# Revit family: Drain_Floor_Round-Zurn-Z415C
name_source: partatom
category: Plumbing Fixtures
units: mm (PartAtom-declared; Revit-internal decimal feet)

## family parameters
Always vertical = Yes
Cut with Voids When Loaded = No
Maintain Annotation Orientation = No
OmniClass Number = 23.70.50.21.24.14
OmniClass Title = Deck Waste Water Drains
Part Type = Normal
Room Calculation Point = No
Round Connector Dimension = Use Radius
Shared = No
Work Plane-Based = No

## types (80) — shared parameters
Assembly Code = D2030300
CW Connection = No
Default Elevation = 30 "
Description = BODY ASSEMBLY W/ “TYPE C” STRAINER
HW Connection = No
Manufacturer = Zurn Water, LLC
Manufacurer Brand = Zurn
Material Main = Iron - Zurn - Cast - Painted - Blue
Modified Date = 12/05/2025
Product Documentation Link = https://files.zurn.com
Product Installation Sheet URL = https://files.zurn.com
Product Page URL = https://www.zurn.com
Product data url = https://bimobject.com
URL = www.zurn.com
Vent Connection = No
Waste Connection = Yes
zero-valued in all types: CWFU, HWFU, WFU

## per-type parameters (varying)
| type | Approx. Wt. Lbs. | Body Height (E) | Grate Radius | Model | Pipe Size 'A' (Inner Diameter) | Pipe Size 'A' (Inner Radius) | Pipe Size 'A' (Nominal Diameter) | Pipe Size 'A' (Nominal Radius) | Pipe Size 'A' (Outer Diameter) | Pipe Size 'A' (Outer Radius) | Strainer Diameter (B) | Strainer Material | Strainer Open Area | Type Comments |
| ZN415C-2IC-5B | 11.00 lb | 4.188 " | 2.2 " | ZN415C | 2.067 " | 1.034 " | 2 " | 1 " | 2.375 " | 1.188 " | 5 " | Bronze - Zurn - Polished Nickel | 8 in² | ZN415C with 5 Inch Strainer and 2 Inch IC Threaed Outlet |
| ZN415C-2IC-6B | 13.00 lb | 4.188 " | 2.7 " | ZN415C | 2.067 " | 1.034 " | 2 " | 1 " | 2.375 " | 1.188 " | 6 " | Bronze - Zurn - Polished Nickel | 9 in² | ZN415C with 6 Inch Strainer and 2 Inch IC Threaed Outlet |
| ZN415C-2IC-7B | 14.00 lb | 4.188 " | 3.2 " | ZN415C | 2.067 " | 1.034 " | 2 " | 1 " | 2.375 " | 1.188 " | 7 " | Bronze - Zurn - Polished Nickel | 13 in² | ZN415C with 7 Inch Strainer and 2 Inch IC Threaed Outlet |
| ZN415C-3IC-5B | 11.00 lb | 4.188 " | 2.2 " | ZN415C | 3.026 " | 1.513 " | 3 " | 1.5 " | 3.5 " | 1.75 " | 5 " | Bronze - Zurn - Polished Nickel | 8 in² | ZN415C with 5 Inch Strainer and 3 Inch IC Threaded Outlet |
| ZN415C-3IC-6B | 13.00 lb | 4.188 " | 2.7 " | ZN415C | 3.026 " | 1.513 " | 3 " | 1.5 " | 3.5 " | 1.75 " | 6 " | Bronze - Zurn - Polished Nickel | 9 in² | ZN415C with 6 Inch Strainer and 3 Inch IC Threaded Outlet |
| ZN415C-3IC-7B | 14.00 lb | 4.188 " | 3.2 " | ZN415C | 3.026 " | 1.513 " | 3 " | 1.5 " | 3.5 " | 1.75 " | 7 " | Bronze - Zurn - Polished Nickel | 13 in² | ZN415C with 7 Inch Strainer and 3 Inch IC Threaded Outlet |
| ZN415C-3IC-8B | 16.00 lb | 4.188 " | 3.7 " | ZN415C | 3.026 " | 1.513 " | 3 " | 1.5 " | 3.5 " | 1.75 " | 8 " | Bronze - Zurn - Polished Nickel | 18 in² | ZN415C with 8 Inch Strainer and 3 Inch IC Threaded Outlet |
| ZN415C-4IC-6B | 13.00 lb | 4.188 " | 2.7 " | ZN415C | 4.028 " | 2.014 " | 4 " | 2 " | 4.5 " | 2.25 " | 6 " | Bronze - Zurn - Polished Nickel | 9 in² | ZN415C with 6 Inch Strainer and 4 Inch IC Threaded Outlet |
| ZN415C-4IC-7B | 14.00 lb | 4.188 " | 3.2 " | ZN415C | 4.028 " | 2.014 " | 4 " | 2 " | 4.5 " | 2.25 " | 7 " | Bronze - Zurn - Polished Nickel | 13 in² | ZN415C with 7 Inch Strainer and 4 Inch IC Threaded Outlet |
| ZN415C-4IC-8B | 16.00 lb | 4.188 " | 3.7 " | ZN415C | 4.028 " | 2.014 " | 4 " | 2 " | 4.5 " | 2.25 " | 8 " | Bronze - Zurn - Polished Nickel | 18 in² | ZN415C with 8 Inch Strainer and 4 Inch IC Threaded Outlet |
| ZN415C-2IP-5B | 11.00 lb | 2.438 " | 2.2 " | ZN415C | 2.067 " | 1.034 " | 2 " | 1 " | 2.375 " | 1.188 " | 5 " | Bronze - Zurn - Polished Nickel | 8 in² | ZN415C with 5 Inch Strainer and 2 Inch IP Threaed Outlet |
| ZN415C-2IP-6B | 13.00 lb | 2.438 " | 2.7 " | ZN415C | 2.067 " | 1.034 " | 2 " | 1 " | 2.375 " | 1.188 " | 6 " | Bronze - Zurn - Polished Nickel | 9 in² | ZN415C with 6 Inch Strainer and 2 Inch IP Threaed Outlet |
| ZN415C-2IP-7B | 14.00 lb | 2.438 " | 3.2 " | ZN415C | 2.067 " | 1.034 " | 2 " | 1 " | 2.375 " | 1.188 " | 7 " | Bronze - Zurn - Polished Nickel | 13 in² | ZN415C with 7 Inch Strainer and 2 Inch IP Threaed Outlet |
| ZN415C-3IP-5B | 11.00 lb | 2.75 " | 2.2 " | ZN415C | 3.026 " | 1.513 " | 3 " | 1.5 " | 3.5 " | 1.75 " | 5 " | Bronze - Zurn - Polished Nickel | 8 in² | ZN415C with 5 Inch Strainer and 3 Inch IP Threaded Outlet |
| ZN415C-3IP-6B | 13.00 lb | 2.75 " | 2.7 " | ZN415C | 3.026 " | 1.513 " | 3 " | 1.5 " | 3.5 " | 1.75 " | 6 " | Bronze - Zurn - Polished Nickel | 9 in² | ZN415C with 6 Inch Strainer and 3 Inch IP Threaded Outlet |
| ZN415C-3IP-7B | 14.00 lb | 2.75 " | 3.2 " | ZN415C | 3.026 " | 1.513 " | 3 " | 1.5 " | 3.5 " | 1.75 " | 7 " | Bronze - Zurn - Polished Nickel | 13 in² | ZN415C with 7 Inch Strainer and 3 Inch IP Threaded Outlet |
| ZN415C-3IP-8B | 16.00 lb | 2.75 " | 3.7 " | ZN415C | 3.026 " | 1.513 " | 3 " | 1.5 " | 3.5 " | 1.75 " | 8 " | Bronze - Zurn - Polished Nickel | 18 in² | ZN415C with 8 Inch Strainer and 3 Inch IP Threaded Outlet |
| ZN415C-4IP-6B | 13.00 lb | 2.813 " | 2.7 " | ZN415C | 4.028 " | 2.014 " | 4 " | 2 " | 4.5 " | 2.25 " | 6 " | Bronze - Zurn - Polished Nickel | 9 in² | ZN415C with 6 Inch Strainer and 4 Inch IP Threaded Outlet |
| ZN415C-4IP-7B | 14.00 lb | 2.813 " | 3.2 " | ZN415C | 4.028 " | 2.014 " | 4 " | 2 " | 4.5 " | 2.25 " | 7 " | Bronze - Zurn - Polished Nickel | 13 in² | ZN415C with 7 Inch Strainer and 4 Inch IP Threaded Outlet |
| ZN415C-4IP-8B | 16.00 lb | 2.813 " | 3.7 " | ZN415C | 4.028 " | 2.014 " | 4 " | 2 " | 4.5 " | 2.25 " | 8 " | Bronze - Zurn - Polished Nickel | 18 in² | ZN415C with 8 Inch Strainer and 4 Inch IP Threaded Outlet |
| ZN415C-6IP-8B | 18.00 lb | 2.875 " | 3.7 " | ZN415C | 6.065 " | 3.033 " | 6 " | 3 " | 6.625 " | 3.313 " | 8 " | Bronze - Zurn - Polished Nickel | 18 in² | ZN415C with 8 Inch Strainer and 6 Inch IP Threaded Outlet |
| ZN415C-2NH-5B | 11.00 lb | 3.813 " | 2.2 " | ZN415C | 2.067 " | 1.034 " | 2 " | 1 " | 2.375 " | 1.188 " | 5 " | Bronze - Zurn - Polished Nickel | 8 in² | ZN415C with 5 Inch Strainer and 2 Inch No-Hub Outlet |
| ZN415C-2NH-6B | 13.00 lb | 3.813 " | 2.7 " | ZN415C | 2.067 " | 1.034 " | 2 " | 1 " | 2.375 " | 1.188 " | 6 " | Bronze - Zurn - Polished Nickel | 9 in² | ZN415C with 6 Inch Strainer and 2 Inch No-Hub Outlet |
| ZN415C-2NH-7B | 14.00 lb | 3.813 " | 3.2 " | ZN415C | 2.067 " | 1.034 " | 2 " | 1 " | 2.375 " | 1.188 " | 7 " | Bronze - Zurn - Polished Nickel | 13 in² | ZN415C with 7 Inch Strainer and 2 Inch No-Hub Outlet |
| ZN415C-3NH-5B | 11.00 lb | 3.813 " | 2.2 " | ZN415C | 3.026 " | 1.513 " | 3 " | 1.5 " | 3.5 " | 1.75 " | 5 " | Bronze - Zurn - Polished Nickel | 8 in² | ZN415C with 5 Inch Strainer and 3 Inch No-Hub Outlet |
| ZN415C-3NH-6B | 13.00 lb | 3.813 " | 2.7 " | ZN415C | 3.026 " | 1.513 " | 3 " | 1.5 " | 3.5 " | 1.75 " | 6 " | Bronze - Zurn - Polished Nickel | 9 in² | ZN415C with 6 Inch Strainer and 3 Inch No-Hub Outlet |
| ZN415C-3NH-7B | 14.00 lb | 3.813 " | 3.2 " | ZN415C | 3.026 " | 1.513 " | 3 " | 1.5 " | 3.5 " | 1.75 " | 7 " | Bronze - Zurn - Polished Nickel | 13 in² | ZN415C with 7 Inch Strainer and 3 Inch No-Hub Outlet |
| ZN415C-3NH-8B | 16.00 lb | 3.813 " | 3.7 " | ZN415C | 3.026 " | 1.513 " | 3 " | 1.5 " | 3.5 " | 1.75 " | 8 " | Bronze - Zurn - Polished Nickel | 18 in² | ZN415C with 8 Inch Strainer and 3 Inch No-Hub Outlet |
| ZN415C-4NH-6B | 13.00 lb | 3.813 " | 2.7 " | ZN415C | 4.028 " | 2.014 " | 4 " | 2 " | 4.5 " | 2.25 " | 6 " | Bronze - Zurn - Polished Nickel | 9 in² | ZN415C with 6 Inch Strainer and 4 Inch No-Hub Outlet |
| ZN415C-4NH-7B | 14.00 lb | 3.813 " | 3.2 " | ZN415C | 4.028 " | 2.014 " | 4 " | 2 " | 4.5 " | 2.25 " | 7 " | Bronze - Zurn - Polished Nickel | 13 in² | ZN415C with 7 Inch Strainer and 4 Inch No-Hub Outlet |
| ZN415C-4NH-8B | 16.00 lb | 3.813 " | 3.7 " | ZN415C | 4.028 " | 2.014 " | 4 " | 2 " | 4.5 " | 2.25 " | 8 " | Bronze - Zurn - Polished Nickel | 18 in² | ZN415C with 8 Inch Strainer and 4 Inch No-Hub Outlet |
| ZN415C-2NL-5B | 11.00 lb | 3.875 " | 2.2 " | ZN415C | 2.067 " | 1.034 " | 2 " | 1 " | 2.375 " | 1.188 " | 5 " | Bronze - Zurn - Polished Nickel | 8 in² | ZN415C with 5 Inch Strainer and 2 Inch Neo-Loc Outlet |
| ZN415C-2NL-6B | 13.00 lb | 3.875 " | 2.7 " | ZN415C | 2.067 " | 1.034 " | 2 " | 1 " | 2.375 " | 1.188 " | 6 " | Bronze - Zurn - Polished Nickel | 9 in² | ZN415C with 6 Inch Strainer and 2 Inch Neo-Loc Outlet |
| ZN415C-2NL-7B | 14.00 lb | 3.875 " | 3.2 " | ZN415C | 2.067 " | 1.034 " | 2 " | 1 " | 2.375 " | 1.188 " | 7 " | Bronze - Zurn - Polished Nickel | 13 in² | ZN415C with 7 Inch Strainer and 2 Inch Neo-Loc Outlet |
| ZN415C-3NL-5B | 11.00 lb | 3.875 " | 2.2 " | ZN415C | 3.026 " | 1.513 " | 3 " | 1.5 " | 3.5 " | 1.75 " | 5 " | Bronze - Zurn - Polished Nickel | 8 in² | ZN415C with 5 Inch Strainer and 3 Inch Neo-Loc Outlet |
| ZN415C-3NL-6B | 13.00 lb | 3.875 " | 2.7 " | ZN415C | 3.026 " | 1.513 " | 3 " | 1.5 " | 3.5 " | 1.75 " | 6 " | Bronze - Zurn - Polished Nickel | 9 in² | ZN415C with 6 Inch Strainer and 3 Inch Neo-Loc Outlet |
| ZN415C-3NL-7B | 14.00 lb | 3.875 " | 3.2 " | ZN415C | 3.026 " | 1.513 " | 3 " | 1.5 " | 3.5 " | 1.75 " | 7 " | Bronze - Zurn - Polished Nickel | 13 in² | ZN415C with 7 Inch Strainer and 3 Inch Neo-Loc Outlet |
| ZN415C-3NL-8B | 16.00 lb | 3.875 " | 3.7 " | ZN415C | 3.026 " | 1.513 " | 3 " | 1.5 " | 3.5 " | 1.75 " | 8 " | Bronze - Zurn - Polished Nickel | 18 in² | ZN415C with 8 Inch Strainer and 3 Inch Neo-Loc Outlet |
| ZN415C-4NL-6B | 13.00 lb | 3.875 " | 2.7 " | ZN415C | 4.028 " | 2.014 " | 4 " | 2 " | 4.5 " | 2.25 " | 6 " | Bronze - Zurn - Polished Nickel | 9 in² | ZN415C with 6 Inch Strainer and 4 Inch Neo-Loc Outlet |
| ZN415C-4NL-7B | 14.00 lb | 3.875 " | 3.2 " | ZN415C | 4.028 " | 2.014 " | 4 " | 2 " | 4.5 " | 2.25 " | 7 " | Bronze - Zurn - Polished Nickel | 13 in² | ZN415C with 7 Inch Strainer and 4 Inch Neo-Loc Outlet |
| ZN415C-4NL-8B | 16.00 lb | 3.875 " | 3.7 " | ZN415C | 4.028 " | 2.014 " | 4 " | 2 " | 4.5 " | 2.25 " | 8 " | Bronze - Zurn - Polished Nickel | 18 in² | ZN415C with 8 Inch Strainer and 4 Inch Neo-Loc Outlet |
| ZB415C-2IC-5B | 11.00 lb | 4.188 " | 2.2 " | ZB415C | 2.067 " | 1.034 " | 2 " | 1 " | 2.375 " | 1.188 " | 5 " | Bronze - Zurn - Polished | 8 in² | ZB415C with 5 Inch Strainer and 2 Inch IC Threaed Outlet |
| ZB415C-2IC-6B | 13.00 lb | 4.188 " | 2.7 " | ZB415C | 2.067 " | 1.034 " | 2 " | 1 " | 2.375 " | 1.188 " | 6 " | Bronze - Zurn - Polished | 9 in² | ZB415C with 6 Inch Strainer and 2 Inch IC Threaed Outlet |
| ZB415C-2IC-7B | 14.00 lb | 4.188 " | 3.2 " | ZB415C | 2.067 " | 1.034 " | 2 " | 1 " | 2.375 " | 1.188 " | 7 " | Bronze - Zurn - Polished | 13 in² | ZB415C with 7 Inch Strainer and 2 Inch IC Threaed Outlet |
| ZB415C-3IC-5B | 11.00 lb | 4.188 " | 2.2 " | ZB415C | 3.026 " | 1.513 " | 3 " | 1.5 " | 3.5 " | 1.75 " | 5 " | Bronze - Zurn - Polished | 8 in² | ZB415C with 5 Inch Strainer and 3 Inch IC Threaded Outlet |
| ZB415C-3IC-6B | 13.00 lb | 4.188 " | 2.7 " | ZB415C | 3.026 " | 1.513 " | 3 " | 1.5 " | 3.5 " | 1.75 " | 6 " | Bronze - Zurn - Polished | 9 in² | ZB415C with 6 Inch Strainer and 3 Inch IC Threaded Outlet |
| ZB415C-3IC-7B | 14.00 lb | 4.188 " | 3.2 " | ZB415C | 3.026 " | 1.513 " | 3 " | 1.5 " | 3.5 " | 1.75 " | 7 " | Bronze - Zurn - Polished | 13 in² | ZB415C with 7 Inch Strainer and 3 Inch IC Threaded Outlet |
| ZB415C-3IC-8B | 16.00 lb | 4.188 " | 3.7 " | ZB415C | 3.026 " | 1.513 " | 3 " | 1.5 " | 3.5 " | 1.75 " | 8 " | Bronze - Zurn - Polished | 18 in² | ZB415C with 8 Inch Strainer and 3 Inch IC Threaded Outlet |
| ZB415C-4IC-6B | 13.00 lb | 4.188 " | 2.7 " | ZB415C | 4.028 " | 2.014 " | 4 " | 2 " | 4.5 " | 2.25 " | 6 " | Bronze - Zurn - Polished | 9 in² | ZB415C with 6 Inch Strainer and 4 Inch IC Threaded Outlet |
| ZB415C-4IC-7B | 14.00 lb | 4.188 " | 3.2 " | ZB415C | 4.028 " | 2.014 " | 4 " | 2 " | 4.5 " | 2.25 " | 7 " | Bronze - Zurn - Polished | 13 in² | ZB415C with 7 Inch Strainer and 4 Inch IC Threaded Outlet |
| ZB415C-4IC-8B | 16.00 lb | 4.188 " | 3.7 " | ZB415C | 4.028 " | 2.014 " | 4 " | 2 " | 4.5 " | 2.25 " | 8 " | Bronze - Zurn - Polished | 18 in² | ZB415C with 8 Inch Strainer and 4 Inch IC Threaded Outlet |
| ZB415C-2IP-5B | 11.00 lb | 2.438 " | 2.2 " | ZB415C | 2.067 " | 1.034 " | 2 " | 1 " | 2.375 " | 1.188 " | 5 " | Bronze - Zurn - Polished | 8 in² | ZB415C with 5 Inch Strainer and 2 Inch IP Threaed Outlet |
| ZB415C-2IP-6B | 13.00 lb | 2.438 " | 2.7 " | ZB415C | 2.067 " | 1.034 " | 2 " | 1 " | 2.375 " | 1.188 " | 6 " | Bronze - Zurn - Polished | 9 in² | ZB415C with 6 Inch Strainer and 2 Inch IP Threaed Outlet |
| ZB415C-2IP-7B | 14.00 lb | 2.438 " | 3.2 " | ZB415C | 2.067 " | 1.034 " | 2 " | 1 " | 2.375 " | 1.188 " | 7 " | Bronze - Zurn - Polished | 13 in² | ZB415C with 7 Inch Strainer and 2 Inch IP Threaed Outlet |
| ZB415C-3IP-5B | 11.00 lb | 2.75 " | 2.2 " | ZB415C | 3.026 " | 1.513 " | 3 " | 1.5 " | 3.5 " | 1.75 " | 5 " | Bronze - Zurn - Polished | 8 in² | ZB415C with 5 Inch Strainer and 3 Inch IP Threaded Outlet |
| ZB415C-3IP-6B | 13.00 lb | 2.75 " | 2.7 " | ZB415C | 3.026 " | 1.513 " | 3 " | 1.5 " | 3.5 " | 1.75 " | 6 " | Bronze - Zurn - Polished | 9 in² | ZB415C with 6 Inch Strainer and 3 Inch IP Threaded Outlet |
| ZB415C-3IP-7B | 14.00 lb | 2.75 " | 3.2 " | ZB415C | 3.026 " | 1.513 " | 3 " | 1.5 " | 3.5 " | 1.75 " | 7 " | Bronze - Zurn - Polished | 13 in² | ZB415C with 7 Inch Strainer and 3 Inch IP Threaded Outlet |
| ZB415C-3IP-8B | 16.00 lb | 2.75 " | 3.7 " | ZB415C | 3.026 " | 1.513 " | 3 " | 1.5 " | 3.5 " | 1.75 " | 8 " | Bronze - Zurn - Polished | 18 in² | ZB415C with 8 Inch Strainer and 3 Inch IP Threaded Outlet |
| ZB415C-4IP-6B | 13.00 lb | 2.813 " | 2.7 " | ZB415C | 4.028 " | 2.014 " | 4 " | 2 " | 4.5 " | 2.25 " | 6 " | Bronze - Zurn - Polished | 9 in² | ZB415C with 6 Inch Strainer and 4 Inch IP Threaded Outlet |
| ZB415C-4IP-7B | 14.00 lb | 2.813 " | 3.2 " | ZB415C | 4.028 " | 2.014 " | 4 " | 2 " | 4.5 " | 2.25 " | 7 " | Bronze - Zurn - Polished | 13 in² | ZB415C with 7 Inch Strainer and 4 Inch IP Threaded Outlet |
| ZB415C-4IP-8B | 16.00 lb | 2.813 " | 3.7 " | ZB415C | 4.028 " | 2.014 " | 4 " | 2 " | 4.5 " | 2.25 " | 8 " | Bronze - Zurn - Polished | 18 in² | ZB415C with 8 Inch Strainer and 4 Inch IP Threaded Outlet |
| ZB415C-6IP-8B | 18.00 lb | 2.875 " | 3.7 " | ZB415C | 6.065 " | 3.033 " | 6 " | 3 " | 6.625 " | 3.313 " | 8 " | Bronze - Zurn - Polished | 18 in² | ZB415C with 8 Inch Strainer and 6 Inch IP Threaded Outlet |
| ZB415C-2NH-7B | 14.00 lb | 3.813 " | 3.2 " | ZB415C | 2.067 " | 1.034 " | 2 " | 1 " | 2.375 " | 1.188 " | 7 " | Bronze - Zurn - Polished | 13 in² | ZB415C with 7 Inch Strainer and 2 Inch No-Hub Outlet |
| ZB415C-3NH-5B | 11.00 lb | 3.813 " | 2.2 " | ZB415C | 3.026 " | 1.513 " | 3 " | 1.5 " | 3.5 " | 1.75 " | 5 " | Bronze - Zurn - Polished | 8 in² | ZB415C with 5 Inch Strainer and 3 Inch No-Hub Outlet |
| ZB415C-3NH-6B | 13.00 lb | 3.813 " | 2.7 " | ZB415C | 3.026 " | 1.513 " | 3 " | 1.5 " | 3.5 " | 1.75 " | 6 " | Bronze - Zurn - Polished | 9 in² | ZB415C with 6 Inch Strainer and 3 Inch No-Hub Outlet |
| ZB415C-3NH-7B | 14.00 lb | 3.813 " | 3.2 " | ZB415C | 3.026 " | 1.513 " | 3 " | 1.5 " | 3.5 " | 1.75 " | 7 " | Bronze - Zurn - Polished | 13 in² | ZB415C with 7 Inch Strainer and 3 Inch No-Hub Outlet |
| ZB415C-3NH-8B | 16.00 lb | 3.813 " | 3.7 " | ZB415C | 3.026 " | 1.513 " | 3 " | 1.5 " | 3.5 " | 1.75 " | 8 " | Bronze - Zurn - Polished | 18 in² | ZB415C with 8 Inch Strainer and 3 Inch No-Hub Outlet |
| ZB415C-4NH-6B | 13.00 lb | 3.813 " | 2.7 " | ZB415C | 4.028 " | 2.014 " | 4 " | 2 " | 4.5 " | 2.25 " | 6 " | Bronze - Zurn - Polished | 9 in² | ZB415C with 6 Inch Strainer and 4 Inch No-Hub Outlet |
| ZB415C-4NH-7B | 14.00 lb | 3.813 " | 3.2 " | ZB415C | 4.028 " | 2.014 " | 4 " | 2 " | 4.5 " | 2.25 " | 7 " | Bronze - Zurn - Polished | 13 in² | ZB415C with 7 Inch Strainer and 4 Inch No-Hub Outlet |
| ZB415C-4NH-8B | 16.00 lb | 3.813 " | 3.7 " | ZB415C | 4.028 " | 2.014 " | 4 " | 2 " | 4.5 " | 2.25 " | 8 " | Bronze - Zurn - Polished | 18 in² | ZB415C with 8 Inch Strainer and 4 Inch No-Hub Outlet |
| ZB415C-2NL-5B | 11.00 lb | 3.875 " | 2.2 " | ZB415C | 2.067 " | 1.034 " | 2 " | 1 " | 2.375 " | 1.188 " | 5 " | Bronze - Zurn - Polished | 8 in² | ZB415C with 5 Inch Strainer and 2 Inch Neo-Loc Outlet |
| ZB415C-2NL-6B | 13.00 lb | 3.875 " | 2.7 " | ZB415C | 2.067 " | 1.034 " | 2 " | 1 " | 2.375 " | 1.188 " | 6 " | Bronze - Zurn - Polished | 9 in² | ZB415C with 6 Inch Strainer and 2 Inch Neo-Loc Outlet |
| ZB415C-2NL-7B | 14.00 lb | 3.875 " | 3.2 " | ZB415C | 2.067 " | 1.034 " | 2 " | 1 " | 2.375 " | 1.188 " | 7 " | Bronze - Zurn - Polished | 13 in² | ZB415C with 7 Inch Strainer and 2 Inch Neo-Loc Outlet |
| ZB415C-3NL-5B | 11.00 lb | 3.875 " | 2.2 " | ZB415C | 3.026 " | 1.513 " | 3 " | 1.5 " | 3.5 " | 1.75 " | 5 " | Bronze - Zurn - Polished | 8 in² | ZB415C with 5 Inch Strainer and 3 Inch Neo-Loc Outlet |
| ZB415C-3NL-6B | 13.00 lb | 3.875 " | 2.7 " | ZB415C | 3.026 " | 1.513 " | 3 " | 1.5 " | 3.5 " | 1.75 " | 6 " | Bronze - Zurn - Polished | 9 in² | ZB415C with 6 Inch Strainer and 3 Inch Neo-Loc Outlet |
| ZB415C-3NL-7B | 14.00 lb | 3.875 " | 3.2 " | ZB415C | 3.026 " | 1.513 " | 3 " | 1.5 " | 3.5 " | 1.75 " | 7 " | Bronze - Zurn - Polished | 13 in² | ZB415C with 7 Inch Strainer and 3 Inch Neo-Loc Outlet |
| ZB415C-3NL-8B | 16.00 lb | 3.875 " | 3.7 " | ZB415C | 3.026 " | 1.513 " | 3 " | 1.5 " | 3.5 " | 1.75 " | 8 " | Bronze - Zurn - Polished | 18 in² | ZB415C with 8 Inch Strainer and 3 Inch Neo-Loc Outlet |
| ZB415C-4NL-6B | 13.00 lb | 3.875 " | 2.7 " | ZB415C | 4.028 " | 2.014 " | 4 " | 2 " | 4.5 " | 2.25 " | 6 " | Bronze - Zurn - Polished | 9 in² | ZB415C with 6 Inch Strainer and 4 Inch Neo-Loc Outlet |
| ZB415C-4NL-7B | 14.00 lb | 3.875 " | 3.2 " | ZB415C | 4.028 " | 2.014 " | 4 " | 2 " | 4.5 " | 2.25 " | 7 " | Bronze - Zurn - Polished | 13 in² | ZB415C with 7 Inch Strainer and 4 Inch Neo-Loc Outlet |
| ZB415C-4NL-8B | 16.00 lb | 3.875 " | 3.7 " | ZB415C | 4.028 " | 2.014 " | 4 " | 2 " | 4.5 " | 2.25 " | 8 " | Bronze - Zurn - Polished | 18 in² | ZB415C with 8 Inch Strainer and 4 Inch Neo-Loc Outlet |

## geometry (parser evidence)
native form markers: Sweep x5
no freeform markers — native parametric forms only
